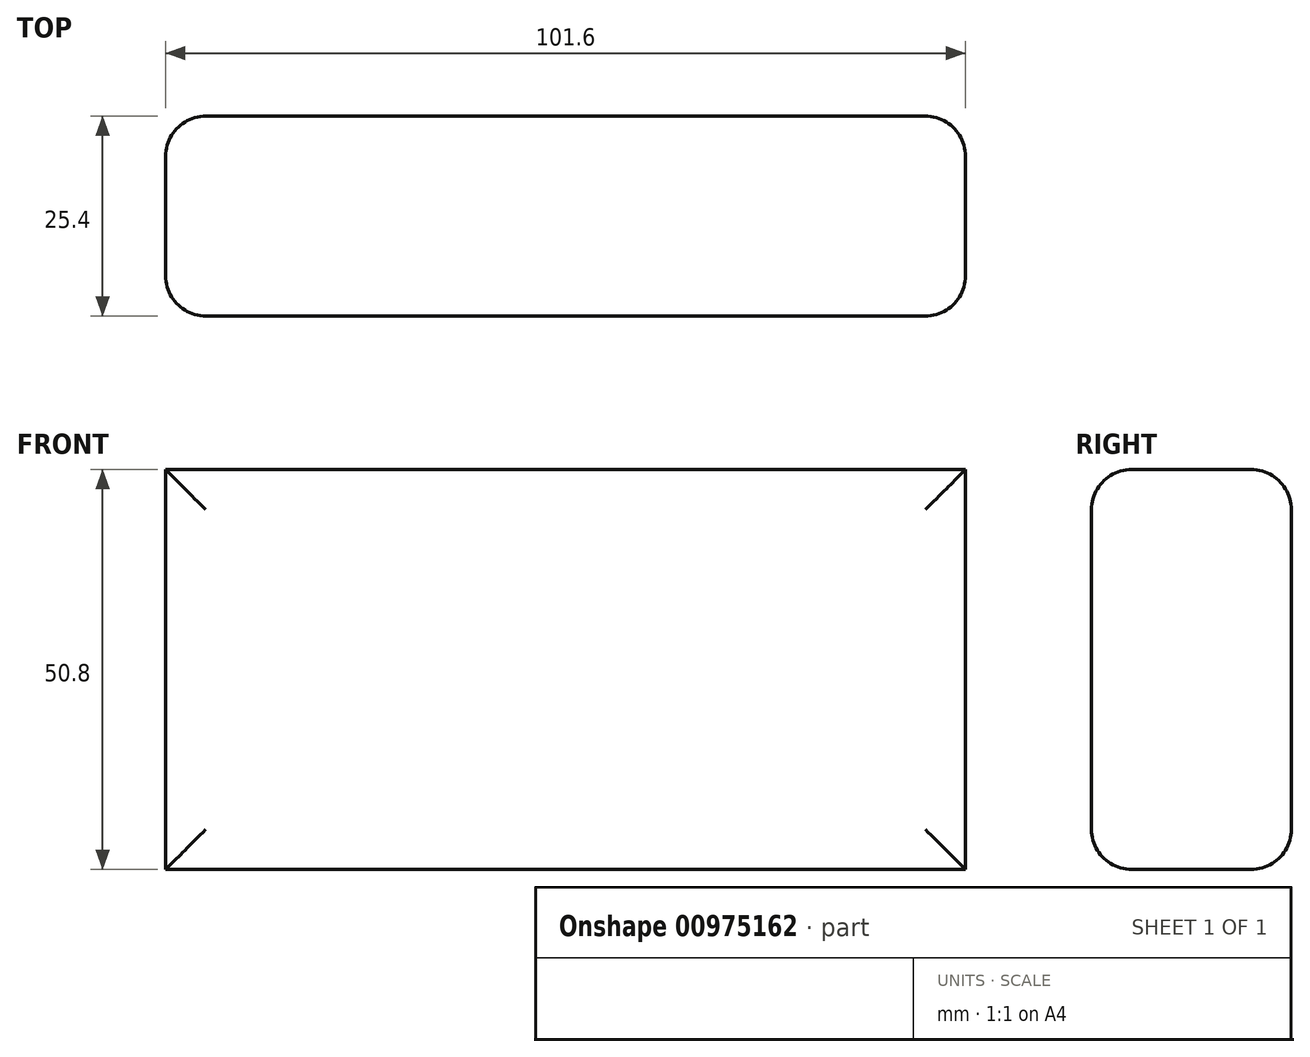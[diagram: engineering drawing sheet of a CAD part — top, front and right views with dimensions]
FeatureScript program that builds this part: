
annotation { "Feature Type Name" : "Feature", "Feature Type Description" : "" }
export const myFeature = defineFeature(function(context is Context, id is Id, definition is map)
    precondition{}
    {
        {
            var Q0;
            Q0=qCreatedBy(makeId("Front.planeOp"),FACE);
            var sketch = newSketch(context, id + "F0", { "sketchPlane" : qUnion([Q0])});
            skLineSegment(sketch, "E0.bottom", {"start": v(-50.8, 25.4) * mm, "end": v(50.8, 25.4) * mm});
            skLineSegment(sketch, "E0.top", {"start": v(-50.8, -25.4) * mm, "end": v(50.8, -25.4) * mm});
            skLineSegment(sketch, "E0.left", {"start": v(-50.8, 25.4) * mm, "end": v(-50.8, -25.4) * mm});
            skLineSegment(sketch, "E0.right", {"start": v(50.8, 25.4) * mm, "end": v(50.8, -25.4) * mm});
            skPoint(sketch, "E0.middle", {"position": v(0, 0) * mm});
            skSolve(sketch);
        }
        {
            var Q0;
            Q0=makeQuery(id+"F0.imprint","IMPRINT",FACE,{"disambiguationData":[TD([[makeQuery(id+"F0.imprint","IMPRINT",EDGE,{"derivedFrom":sQuery(id+"F0.wireOp",EDGE,"E0.bottom")}),-1.0]])]});
            extrude(context, id + "F1", {"entities" : qUnion([Q0]), "depth" : 25.4 * mm, "offsetDistance" : 25.4 * mm});
        }
        {
            var Q0;
            Q0=makeQuery(id+"F1.opExtrude","CAP_FACE",FACE,{"disambiguationData":[OSD([sQuery(id+"F0.wireOp",EDGE,"E0.bottom"),sQuery(id+"F0.wireOp",EDGE,"E0.top"),sQuery(id+"F0.wireOp",EDGE,"E0.left"),sQuery(id+"F0.wireOp",EDGE,"E0.right")])],"isStart":false});
            fillet(context, id + "F2", {"entities" : qUnion([Q0]), "radius" : 5.08 * mm, "tangentPropagation" : true, "allowEdgeOverflow" : false});
        }
        {
            var Q0;
            Q0=makeQuery(id+"F1.opExtrude","CAP_FACE",FACE,{"disambiguationData":[OSD([sQuery(id+"F0.wireOp",EDGE,"E0.bottom"),sQuery(id+"F0.wireOp",EDGE,"E0.top"),sQuery(id+"F0.wireOp",EDGE,"E0.left"),sQuery(id+"F0.wireOp",EDGE,"E0.right")])],"isStart":true});
            fillet(context, id + "F3", {"entities" : qUnion([Q0]), "radius" : 5.08 * mm, "tangentPropagation" : true, "allowEdgeOverflow" : false});
        }
    });
